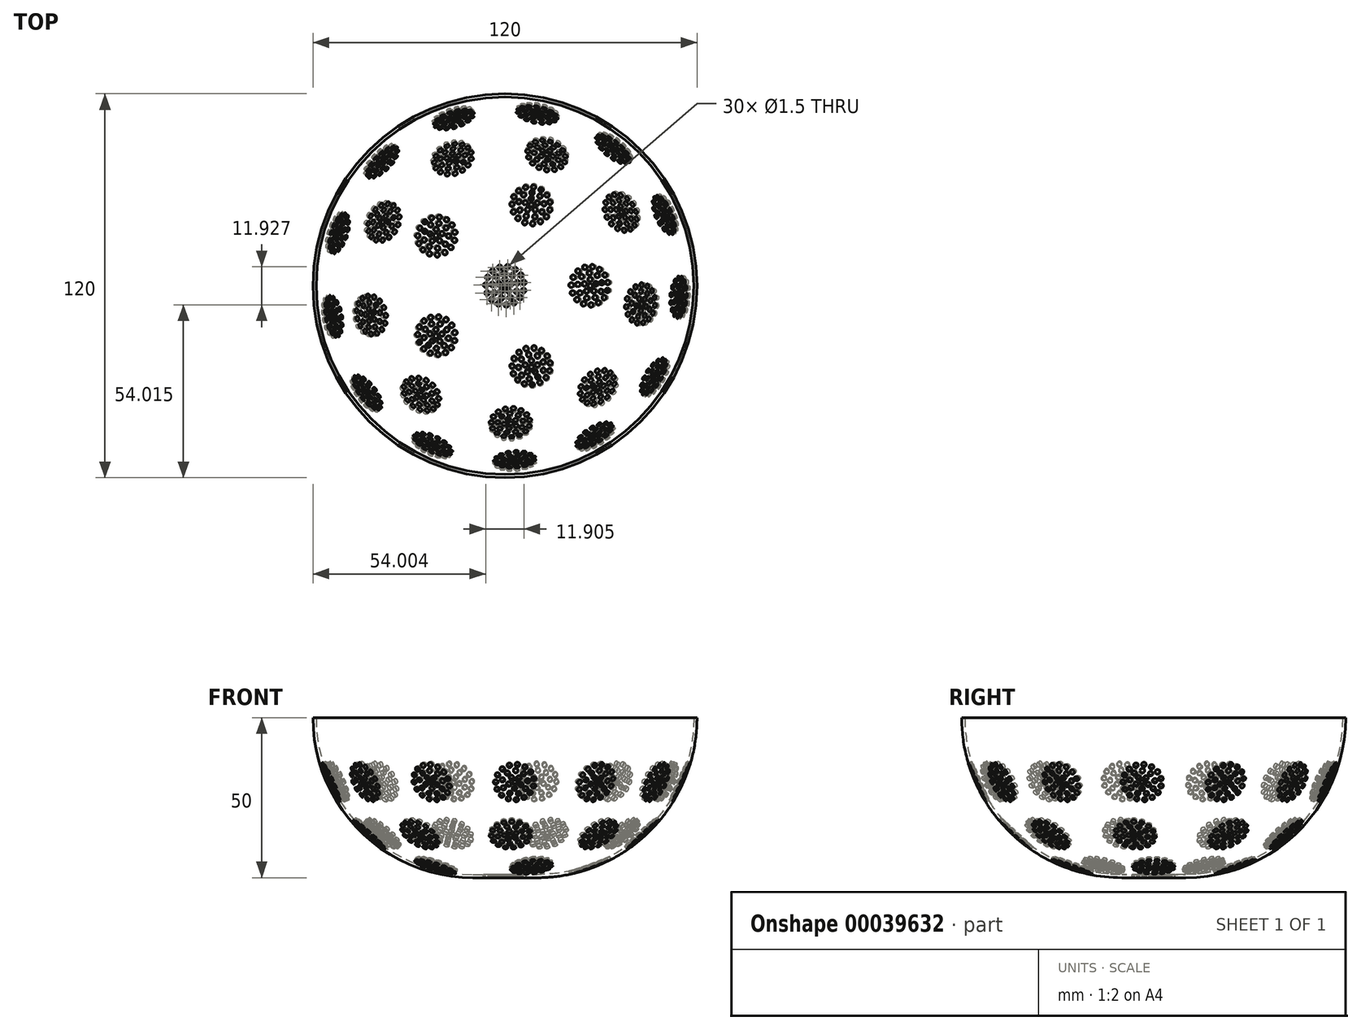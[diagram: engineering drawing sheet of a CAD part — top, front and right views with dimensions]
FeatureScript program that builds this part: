
annotation { "Feature Type Name" : "Feature", "Feature Type Description" : "" }
export const myFeature = defineFeature(function(context is Context, id is Id, definition is map)
    precondition{}
    {
        {
            var Q0;
            Q0=qCreatedBy(makeId("Front.planeOp"),FACE);
            var sketch = newSketch(context, id + "F0", { "sketchPlane" : qUnion([Q0])});
            skLineSegment(sketch, "E0", {"start": v(0, 0) * mm, "end": v(10, 0) * mm});
            skArc(sketch, "E1", {"start": v(10, 0) * mm, "mid": v(45.36, 14.64) * mm, "end": v(60, 50) * mm});
            skLineSegment(sketch, "E2", {"start": v(0, 0) * mm, "end": v(0, 50) * mm});
            skLineSegment(sketch, "E3", {"start": v(0, 50) * mm, "end": v(60, 50) * mm});
            skArc(sketch, "E4.0", {"start": v(10, 1) * mm, "mid": v(44.65, 15.35) * mm, "end": v(59, 50) * mm});
            skLineSegment(sketch, "E4.1", {"start": v(0, 1) * mm, "end": v(10, 1) * mm});
            skSolve(sketch);
        }
        {
            var Q0;
            {var subQ2=sQuery(id+"F0.wireOp",EDGE,"E0");Q0=makeQuery(id+"F0.imprint","IMPRINT",FACE,{"disambiguationData":[TD([[makeQuery(id+"F0.imprint","IMPRINT",EDGE,{"derivedFrom":subQ2}),1.0]])]});}
            var Q1;
            Q1=sQuery(id+"F0.wireOp",EDGE,"E2");
            revolve(context, id + "F1", {"entities" : qUnion([Q0]), "axis" : qUnion([Q1]), "revolveType" : RevolveType.FULL});
        }
        {
            var Q0;
            Q0=makeQuery(id+"F1.opRevolve","SWEPT_FACE",FACE,{"disambiguationData":[OSD([sQuery(id+"F0.wireOp",EDGE,"E4.1")])]});
            var sketch = newSketch(context, id + "F2", { "sketchPlane" : qUnion([Q0])});
            skCircle(sketch, "E5", {"center": v(0, 0) * mm, "radius": 0.75 * mm});
            skCircle(sketch, "E6", {"center": v(0, 2) * mm, "radius": 0.75 * mm});
            skCircle(sketch, "E7.1.0", {"center": v(-1.9, 0.62) * mm, "radius": 0.75 * mm});
            skCircle(sketch, "E7.2.0", {"center": v(-1.18, -1.62) * mm, "radius": 0.75 * mm});
            skCircle(sketch, "E7.3.0", {"center": v(1.18, -1.62) * mm, "radius": 0.75 * mm});
            skCircle(sketch, "E7.4.0", {"center": v(1.9, 0.62) * mm, "radius": 0.75 * mm});
            skLineSegment(sketch, "E8", {"start": v(0, 2) * mm, "end": v(1.9, 0.62) * mm, "construction": true});
            skLineSegment(sketch, "E9", {"start": v(0, 0) * mm, "end": v(0.95, 1.3) * mm, "construction": true});
            skLineSegment(sketch, "E10", {"start": v(0.95, 1.3) * mm, "end": v(2.35, 3.24) * mm, "construction": true});
            skCircle(sketch, "E11", {"center": v(2.35, 3.24) * mm, "radius": 0.75 * mm});
            skCircle(sketch, "E12.1.0", {"center": v(-0.28, 4) * mm, "radius": 0.75 * mm});
            skCircle(sketch, "E12.2.0", {"center": v(-2.78, 2.88) * mm, "radius": 0.75 * mm});
            skCircle(sketch, "E12.3.0", {"center": v(-3.98, 0.42) * mm, "radius": 0.75 * mm});
            skCircle(sketch, "E12.4.0", {"center": v(-3.32, -2.24) * mm, "radius": 0.75 * mm});
            skCircle(sketch, "E12.5.0", {"center": v(-1.1, -3.85) * mm, "radius": 0.75 * mm});
            skCircle(sketch, "E12.6.0", {"center": v(1.63, -3.65) * mm, "radius": 0.75 * mm});
            skCircle(sketch, "E13.1.7.0", {"center": v(3.6, -1.75) * mm, "radius": 0.75 * mm});
            skCircle(sketch, "E13.1.8.0", {"center": v(3.88, 0.97) * mm, "radius": 0.75 * mm});
            skLineSegment(sketch, "E14", {"start": v(3.88, 0.97) * mm, "end": v(2.35, 3.24) * mm, "construction": true});
            skLineSegment(sketch, "E15", {"start": v(0, 0) * mm, "end": v(3.12, 2.1) * mm, "construction": true});
            skLineSegment(sketch, "E16", {"start": v(3.12, 2.1) * mm, "end": v(4.97, 3.36) * mm, "construction": true});
            skCircle(sketch, "E17", {"center": v(4.97, 3.36) * mm, "radius": 0.75 * mm});
            skCircle(sketch, "E18.1.0", {"center": v(3.18, 5.09) * mm, "radius": 0.75 * mm});
            skCircle(sketch, "E18.2.0", {"center": v(0.84, 5.94) * mm, "radius": 0.75 * mm});
            skCircle(sketch, "E18.3.0", {"center": v(-1.65, 5.77) * mm, "radius": 0.75 * mm});
            skCircle(sketch, "E18.4.0", {"center": v(-3.86, 4.6) * mm, "radius": 0.75 * mm});
            skCircle(sketch, "E18.5.0", {"center": v(-5.4, 2.63) * mm, "radius": 0.75 * mm});
            skCircle(sketch, "E18.6.0", {"center": v(-6, 0.2) * mm, "radius": 0.75 * mm});
            skCircle(sketch, "E18.7.0", {"center": v(-5.56, -2.25) * mm, "radius": 0.75 * mm});
            skCircle(sketch, "E18.8.0", {"center": v(-4.17, -4.32) * mm, "radius": 0.75 * mm});
            skCircle(sketch, "E18.9.0", {"center": v(-2.05, -5.64) * mm, "radius": 0.75 * mm});
            skCircle(sketch, "E18.10.0", {"center": v(0.42, -5.99) * mm, "radius": 0.75 * mm});
            skCircle(sketch, "E18.11.0", {"center": v(2.82, -5.3) * mm, "radius": 0.75 * mm});
            skCircle(sketch, "E18.12.0", {"center": v(4.73, -3.7) * mm, "radius": 0.75 * mm});
            skCircle(sketch, "E18.13.0", {"center": v(5.82, -1.45) * mm, "radius": 0.75 * mm});
            skCircle(sketch, "E18.14.0", {"center": v(5.9, 1.04) * mm, "radius": 0.75 * mm});
            skSolve(sketch);
        }
        {
            var Q0;
            Q0 = qSketchRegion(id + "F2", true);
            extrude(context, id + "F3", {"entities" : qUnion([Q0]), "operationType" : NewBodyOperationType.REMOVE, "oppositeDirection" : true, "depth" : 25 * mm});
        }
        {
            var Q0;
            Q0=makeQuery(id+"F1.opRevolve","SWEPT_FACE",FACE,{"disambiguationData":[OSD([sQuery(id+"F0.wireOp",EDGE,"E3")])]});
            var sketch = newSketch(context, id + "F4", { "sketchPlane" : qUnion([Q0])});
            skLineSegment(sketch, "E19", {"start": v(0, 59) * mm, "end": v(0, -59) * mm});
            skLineSegment(sketch, "E20", {"start": v(0, 0) * mm, "end": v(-31.56, 49.85) * mm});
            skLineSegment(sketch, "E21", {"start": v(0, 0) * mm, "end": v(-46.28, 36.6) * mm});
            skSolve(sketch);
        }
        {
            var Q0;
            Q0=makeQuery(id+"F3.boolean.opBoolean","COPY",FACE,{"derivedFrom":makeQuery(id+"F3.opExtrude","SWEPT_FACE",FACE,{"disambiguationData":[OSD([sQuery(id+"F2.wireOp",EDGE,"E18.7.0")])]})});
            var Q1;
            Q1=makeQuery(id+"F3.boolean.opBoolean","COPY",FACE,{"derivedFrom":makeQuery(id+"F3.opExtrude","SWEPT_FACE",FACE,{"disambiguationData":[OSD([sQuery(id+"F2.wireOp",EDGE,"E18.6.0")])]})});
            var Q2;
            Q2=makeQuery(id+"F3.boolean.opBoolean","COPY",FACE,{"derivedFrom":makeQuery(id+"F3.opExtrude","SWEPT_FACE",FACE,{"disambiguationData":[OSD([sQuery(id+"F2.wireOp",EDGE,"E18.5.0")])]})});
            var Q3;
            Q3=makeQuery(id+"F3.boolean.opBoolean","COPY",FACE,{"derivedFrom":makeQuery(id+"F3.opExtrude","SWEPT_FACE",FACE,{"disambiguationData":[OSD([sQuery(id+"F2.wireOp",EDGE,"E18.4.0")])]})});
            var Q4;
            Q4=makeQuery(id+"F3.boolean.opBoolean","COPY",FACE,{"derivedFrom":makeQuery(id+"F3.opExtrude","SWEPT_FACE",FACE,{"disambiguationData":[OSD([sQuery(id+"F2.wireOp",EDGE,"E18.3.0")])]})});
            var Q5;
            Q5=makeQuery(id+"F3.boolean.opBoolean","COPY",FACE,{"derivedFrom":makeQuery(id+"F3.opExtrude","SWEPT_FACE",FACE,{"disambiguationData":[OSD([sQuery(id+"F2.wireOp",EDGE,"E18.2.0")])]})});
            var Q6;
            Q6=makeQuery(id+"F3.boolean.opBoolean","COPY",FACE,{"derivedFrom":makeQuery(id+"F3.opExtrude","SWEPT_FACE",FACE,{"disambiguationData":[OSD([sQuery(id+"F2.wireOp",EDGE,"E18.1.0")])]})});
            var Q7;
            Q7=makeQuery(id+"F3.boolean.opBoolean","COPY",FACE,{"derivedFrom":makeQuery(id+"F3.opExtrude","SWEPT_FACE",FACE,{"disambiguationData":[OSD([sQuery(id+"F2.wireOp",EDGE,"E17")])]})});
            var Q8;
            Q8=makeQuery(id+"F3.boolean.opBoolean","COPY",FACE,{"derivedFrom":makeQuery(id+"F3.opExtrude","SWEPT_FACE",FACE,{"disambiguationData":[OSD([sQuery(id+"F2.wireOp",EDGE,"E18.14.0")])]})});
            var Q9;
            Q9=makeQuery(id+"F3.boolean.opBoolean","COPY",FACE,{"derivedFrom":makeQuery(id+"F3.opExtrude","SWEPT_FACE",FACE,{"disambiguationData":[OSD([sQuery(id+"F2.wireOp",EDGE,"E18.13.0")])]})});
            var Q10;
            Q10=makeQuery(id+"F3.boolean.opBoolean","COPY",FACE,{"derivedFrom":makeQuery(id+"F3.opExtrude","SWEPT_FACE",FACE,{"disambiguationData":[OSD([sQuery(id+"F2.wireOp",EDGE,"E18.12.0")])]})});
            var Q11;
            Q11=makeQuery(id+"F3.boolean.opBoolean","COPY",FACE,{"derivedFrom":makeQuery(id+"F3.opExtrude","SWEPT_FACE",FACE,{"disambiguationData":[OSD([sQuery(id+"F2.wireOp",EDGE,"E18.11.0")])]})});
            var Q12;
            Q12=makeQuery(id+"F3.boolean.opBoolean","COPY",FACE,{"derivedFrom":makeQuery(id+"F3.opExtrude","SWEPT_FACE",FACE,{"disambiguationData":[OSD([sQuery(id+"F2.wireOp",EDGE,"E18.10.0")])]})});
            var Q13;
            Q13=makeQuery(id+"F3.boolean.opBoolean","COPY",FACE,{"derivedFrom":makeQuery(id+"F3.opExtrude","SWEPT_FACE",FACE,{"disambiguationData":[OSD([sQuery(id+"F2.wireOp",EDGE,"E18.9.0")])]})});
            var Q14;
            Q14=makeQuery(id+"F3.boolean.opBoolean","COPY",FACE,{"derivedFrom":makeQuery(id+"F3.opExtrude","SWEPT_FACE",FACE,{"disambiguationData":[OSD([sQuery(id+"F2.wireOp",EDGE,"E18.8.0")])]})});
            var Q15;
            Q15=makeQuery(id+"F3.boolean.opBoolean","COPY",FACE,{"derivedFrom":makeQuery(id+"F3.opExtrude","SWEPT_FACE",FACE,{"disambiguationData":[OSD([sQuery(id+"F2.wireOp",EDGE,"E12.4.0")])]})});
            var Q16;
            Q16=makeQuery(id+"F3.boolean.opBoolean","COPY",FACE,{"derivedFrom":makeQuery(id+"F3.opExtrude","SWEPT_FACE",FACE,{"disambiguationData":[OSD([sQuery(id+"F2.wireOp",EDGE,"E12.3.0")])]})});
            var Q17;
            Q17=makeQuery(id+"F3.boolean.opBoolean","COPY",FACE,{"derivedFrom":makeQuery(id+"F3.opExtrude","SWEPT_FACE",FACE,{"disambiguationData":[OSD([sQuery(id+"F2.wireOp",EDGE,"E12.2.0")])]})});
            var Q18;
            Q18=makeQuery(id+"F3.boolean.opBoolean","COPY",FACE,{"derivedFrom":makeQuery(id+"F3.opExtrude","SWEPT_FACE",FACE,{"disambiguationData":[OSD([sQuery(id+"F2.wireOp",EDGE,"E12.1.0")])]})});
            var Q19;
            Q19=makeQuery(id+"F3.boolean.opBoolean","COPY",FACE,{"derivedFrom":makeQuery(id+"F3.opExtrude","SWEPT_FACE",FACE,{"disambiguationData":[OSD([sQuery(id+"F2.wireOp",EDGE,"E11")])]})});
            var Q20;
            Q20=makeQuery(id+"F3.boolean.opBoolean","COPY",FACE,{"derivedFrom":makeQuery(id+"F3.opExtrude","SWEPT_FACE",FACE,{"disambiguationData":[OSD([sQuery(id+"F2.wireOp",EDGE,"E13.1.8.0")])]})});
            var Q21;
            Q21=makeQuery(id+"F3.boolean.opBoolean","COPY",FACE,{"derivedFrom":makeQuery(id+"F3.opExtrude","SWEPT_FACE",FACE,{"disambiguationData":[OSD([sQuery(id+"F2.wireOp",EDGE,"E13.1.7.0")])]})});
            var Q22;
            Q22=makeQuery(id+"F3.boolean.opBoolean","COPY",FACE,{"derivedFrom":makeQuery(id+"F3.opExtrude","SWEPT_FACE",FACE,{"disambiguationData":[OSD([sQuery(id+"F2.wireOp",EDGE,"E12.6.0")])]})});
            var Q23;
            Q23=makeQuery(id+"F3.boolean.opBoolean","COPY",FACE,{"derivedFrom":makeQuery(id+"F3.opExtrude","SWEPT_FACE",FACE,{"disambiguationData":[OSD([sQuery(id+"F2.wireOp",EDGE,"E12.5.0")])]})});
            var Q24;
            Q24=makeQuery(id+"F3.boolean.opBoolean","COPY",FACE,{"derivedFrom":makeQuery(id+"F3.opExtrude","SWEPT_FACE",FACE,{"disambiguationData":[OSD([sQuery(id+"F2.wireOp",EDGE,"E7.2.0")])]})});
            var Q25;
            Q25=makeQuery(id+"F3.boolean.opBoolean","COPY",FACE,{"derivedFrom":makeQuery(id+"F3.opExtrude","SWEPT_FACE",FACE,{"disambiguationData":[OSD([sQuery(id+"F2.wireOp",EDGE,"E7.1.0")])]})});
            var Q26;
            Q26=makeQuery(id+"F3.boolean.opBoolean","COPY",FACE,{"derivedFrom":makeQuery(id+"F3.opExtrude","SWEPT_FACE",FACE,{"disambiguationData":[OSD([sQuery(id+"F2.wireOp",EDGE,"E6")])]})});
            var Q27;
            Q27=makeQuery(id+"F3.boolean.opBoolean","COPY",FACE,{"derivedFrom":makeQuery(id+"F3.opExtrude","SWEPT_FACE",FACE,{"disambiguationData":[OSD([sQuery(id+"F2.wireOp",EDGE,"E7.4.0")])]})});
            var Q28;
            Q28=makeQuery(id+"F3.boolean.opBoolean","COPY",FACE,{"derivedFrom":makeQuery(id+"F3.opExtrude","SWEPT_FACE",FACE,{"disambiguationData":[OSD([sQuery(id+"F2.wireOp",EDGE,"E7.3.0")])]})});
            var Q29;
            Q29=makeQuery(id+"F3.boolean.opBoolean","COPY",FACE,{"derivedFrom":makeQuery(id+"F3.opExtrude","SWEPT_FACE",FACE,{"disambiguationData":[OSD([sQuery(id+"F2.wireOp",EDGE,"E5")])]})});
            var Q30;
            Q30=sQuery(id+"F4.wireOp",EDGE,"E19");
            circularPattern(context, id + "F5", {"faces" : qUnion([Q0, Q1, Q2, Q3, Q4, Q5, Q6, Q7, Q8, Q9, Q10, Q11, Q12, Q13, Q14, Q15, Q16, Q17, Q18, Q19, Q20, Q21, Q22, Q23, Q24, Q25, Q26, Q27, Q28, Q29]), "axis" : qUnion([Q30]), "angle" : 30 * degree, "instanceCount" : 2, "patternType" : PatternType.FACE});
        }
        {
            var Q0;
            Q0=makeQuery(id+"F5.opPattern","COPY",FACE,{"derivedFrom":makeQuery(id+"F3.boolean.opBoolean","COPY",FACE,{"derivedFrom":makeQuery(id+"F3.opExtrude","SWEPT_FACE",FACE,{"disambiguationData":[OSD([sQuery(id+"F2.wireOp",EDGE,"E18.5.0")])]})}),"instanceName":"1"});
            var Q1;
            Q1=makeQuery(id+"F5.opPattern","COPY",FACE,{"derivedFrom":makeQuery(id+"F3.boolean.opBoolean","COPY",FACE,{"derivedFrom":makeQuery(id+"F3.opExtrude","SWEPT_FACE",FACE,{"disambiguationData":[OSD([sQuery(id+"F2.wireOp",EDGE,"E18.6.0")])]})}),"instanceName":"1"});
            var Q2;
            Q2=makeQuery(id+"F5.opPattern","COPY",FACE,{"derivedFrom":makeQuery(id+"F3.boolean.opBoolean","COPY",FACE,{"derivedFrom":makeQuery(id+"F3.opExtrude","SWEPT_FACE",FACE,{"disambiguationData":[OSD([sQuery(id+"F2.wireOp",EDGE,"E18.7.0")])]})}),"instanceName":"1"});
            var Q3;
            Q3=makeQuery(id+"F5.opPattern","COPY",FACE,{"derivedFrom":makeQuery(id+"F3.boolean.opBoolean","COPY",FACE,{"derivedFrom":makeQuery(id+"F3.opExtrude","SWEPT_FACE",FACE,{"disambiguationData":[OSD([sQuery(id+"F2.wireOp",EDGE,"E18.8.0")])]})}),"instanceName":"1"});
            var Q4;
            Q4=makeQuery(id+"F5.opPattern","COPY",FACE,{"derivedFrom":makeQuery(id+"F3.boolean.opBoolean","COPY",FACE,{"derivedFrom":makeQuery(id+"F3.opExtrude","SWEPT_FACE",FACE,{"disambiguationData":[OSD([sQuery(id+"F2.wireOp",EDGE,"E18.9.0")])]})}),"instanceName":"1"});
            var Q5;
            Q5=makeQuery(id+"F5.opPattern","COPY",FACE,{"derivedFrom":makeQuery(id+"F3.boolean.opBoolean","COPY",FACE,{"derivedFrom":makeQuery(id+"F3.opExtrude","SWEPT_FACE",FACE,{"disambiguationData":[OSD([sQuery(id+"F2.wireOp",EDGE,"E18.11.0")])]})}),"instanceName":"1"});
            var Q6;
            Q6=makeQuery(id+"F5.opPattern","COPY",FACE,{"derivedFrom":makeQuery(id+"F3.boolean.opBoolean","COPY",FACE,{"derivedFrom":makeQuery(id+"F3.opExtrude","SWEPT_FACE",FACE,{"disambiguationData":[OSD([sQuery(id+"F2.wireOp",EDGE,"E18.12.0")])]})}),"instanceName":"1"});
            var Q7;
            Q7=makeQuery(id+"F5.opPattern","COPY",FACE,{"derivedFrom":makeQuery(id+"F3.boolean.opBoolean","COPY",FACE,{"derivedFrom":makeQuery(id+"F3.opExtrude","SWEPT_FACE",FACE,{"disambiguationData":[OSD([sQuery(id+"F2.wireOp",EDGE,"E18.13.0")])]})}),"instanceName":"1"});
            var Q8;
            Q8=makeQuery(id+"F5.opPattern","COPY",FACE,{"derivedFrom":makeQuery(id+"F3.boolean.opBoolean","COPY",FACE,{"derivedFrom":makeQuery(id+"F3.opExtrude","SWEPT_FACE",FACE,{"disambiguationData":[OSD([sQuery(id+"F2.wireOp",EDGE,"E18.14.0")])]})}),"instanceName":"1"});
            var Q9;
            Q9=makeQuery(id+"F5.opPattern","COPY",FACE,{"derivedFrom":makeQuery(id+"F3.boolean.opBoolean","COPY",FACE,{"derivedFrom":makeQuery(id+"F3.opExtrude","SWEPT_FACE",FACE,{"disambiguationData":[OSD([sQuery(id+"F2.wireOp",EDGE,"E17")])]})}),"instanceName":"1"});
            var Q10;
            Q10=makeQuery(id+"F5.opPattern","COPY",FACE,{"derivedFrom":makeQuery(id+"F3.boolean.opBoolean","COPY",FACE,{"derivedFrom":makeQuery(id+"F3.opExtrude","SWEPT_FACE",FACE,{"disambiguationData":[OSD([sQuery(id+"F2.wireOp",EDGE,"E18.1.0")])]})}),"instanceName":"1"});
            var Q11;
            Q11=makeQuery(id+"F5.opPattern","COPY",FACE,{"derivedFrom":makeQuery(id+"F3.boolean.opBoolean","COPY",FACE,{"derivedFrom":makeQuery(id+"F3.opExtrude","SWEPT_FACE",FACE,{"disambiguationData":[OSD([sQuery(id+"F2.wireOp",EDGE,"E18.2.0")])]})}),"instanceName":"1"});
            var Q12;
            Q12=makeQuery(id+"F5.opPattern","COPY",FACE,{"derivedFrom":makeQuery(id+"F3.boolean.opBoolean","COPY",FACE,{"derivedFrom":makeQuery(id+"F3.opExtrude","SWEPT_FACE",FACE,{"disambiguationData":[OSD([sQuery(id+"F2.wireOp",EDGE,"E18.3.0")])]})}),"instanceName":"1"});
            var Q13;
            Q13=makeQuery(id+"F5.opPattern","COPY",FACE,{"derivedFrom":makeQuery(id+"F3.boolean.opBoolean","COPY",FACE,{"derivedFrom":makeQuery(id+"F3.opExtrude","SWEPT_FACE",FACE,{"disambiguationData":[OSD([sQuery(id+"F2.wireOp",EDGE,"E18.4.0")])]})}),"instanceName":"1"});
            var Q14;
            Q14=makeQuery(id+"F5.opPattern","COPY",FACE,{"derivedFrom":makeQuery(id+"F3.boolean.opBoolean","COPY",FACE,{"derivedFrom":makeQuery(id+"F3.opExtrude","SWEPT_FACE",FACE,{"disambiguationData":[OSD([sQuery(id+"F2.wireOp",EDGE,"E12.2.0")])]})}),"instanceName":"1"});
            var Q15;
            Q15=makeQuery(id+"F5.opPattern","COPY",FACE,{"derivedFrom":makeQuery(id+"F3.boolean.opBoolean","COPY",FACE,{"derivedFrom":makeQuery(id+"F3.opExtrude","SWEPT_FACE",FACE,{"disambiguationData":[OSD([sQuery(id+"F2.wireOp",EDGE,"E12.3.0")])]})}),"instanceName":"1"});
            var Q16;
            Q16=makeQuery(id+"F5.opPattern","COPY",FACE,{"derivedFrom":makeQuery(id+"F3.boolean.opBoolean","COPY",FACE,{"derivedFrom":makeQuery(id+"F3.opExtrude","SWEPT_FACE",FACE,{"disambiguationData":[OSD([sQuery(id+"F2.wireOp",EDGE,"E12.4.0")])]})}),"instanceName":"1"});
            var Q17;
            Q17=makeQuery(id+"F5.opPattern","COPY",FACE,{"derivedFrom":makeQuery(id+"F3.boolean.opBoolean","COPY",FACE,{"derivedFrom":makeQuery(id+"F3.opExtrude","SWEPT_FACE",FACE,{"disambiguationData":[OSD([sQuery(id+"F2.wireOp",EDGE,"E12.6.0")])]})}),"instanceName":"1"});
            var Q18;
            Q18=makeQuery(id+"F5.opPattern","COPY",FACE,{"derivedFrom":makeQuery(id+"F3.boolean.opBoolean","COPY",FACE,{"derivedFrom":makeQuery(id+"F3.opExtrude","SWEPT_FACE",FACE,{"disambiguationData":[OSD([sQuery(id+"F2.wireOp",EDGE,"E13.1.7.0")])]})}),"instanceName":"1"});
            var Q19;
            Q19=makeQuery(id+"F5.opPattern","COPY",FACE,{"derivedFrom":makeQuery(id+"F3.boolean.opBoolean","COPY",FACE,{"derivedFrom":makeQuery(id+"F3.opExtrude","SWEPT_FACE",FACE,{"disambiguationData":[OSD([sQuery(id+"F2.wireOp",EDGE,"E18.10.0")])]})}),"instanceName":"1"});
            var Q20;
            Q20=makeQuery(id+"F5.opPattern","COPY",FACE,{"derivedFrom":makeQuery(id+"F3.boolean.opBoolean","COPY",FACE,{"derivedFrom":makeQuery(id+"F3.opExtrude","SWEPT_FACE",FACE,{"disambiguationData":[OSD([sQuery(id+"F2.wireOp",EDGE,"E12.5.0")])]})}),"instanceName":"1"});
            var Q21;
            Q21=makeQuery(id+"F5.opPattern","COPY",FACE,{"derivedFrom":makeQuery(id+"F3.boolean.opBoolean","COPY",FACE,{"derivedFrom":makeQuery(id+"F3.opExtrude","SWEPT_FACE",FACE,{"disambiguationData":[OSD([sQuery(id+"F2.wireOp",EDGE,"E7.2.0")])]})}),"instanceName":"1"});
            var Q22;
            Q22=makeQuery(id+"F5.opPattern","COPY",FACE,{"derivedFrom":makeQuery(id+"F3.boolean.opBoolean","COPY",FACE,{"derivedFrom":makeQuery(id+"F3.opExtrude","SWEPT_FACE",FACE,{"disambiguationData":[OSD([sQuery(id+"F2.wireOp",EDGE,"E5")])]})}),"instanceName":"1"});
            var Q23;
            Q23=makeQuery(id+"F5.opPattern","COPY",FACE,{"derivedFrom":makeQuery(id+"F3.boolean.opBoolean","COPY",FACE,{"derivedFrom":makeQuery(id+"F3.opExtrude","SWEPT_FACE",FACE,{"disambiguationData":[OSD([sQuery(id+"F2.wireOp",EDGE,"E6")])]})}),"instanceName":"1"});
            var Q24;
            Q24=makeQuery(id+"F5.opPattern","COPY",FACE,{"derivedFrom":makeQuery(id+"F3.boolean.opBoolean","COPY",FACE,{"derivedFrom":makeQuery(id+"F3.opExtrude","SWEPT_FACE",FACE,{"disambiguationData":[OSD([sQuery(id+"F2.wireOp",EDGE,"E7.4.0")])]})}),"instanceName":"1"});
            var Q25;
            Q25=makeQuery(id+"F5.opPattern","COPY",FACE,{"derivedFrom":makeQuery(id+"F3.boolean.opBoolean","COPY",FACE,{"derivedFrom":makeQuery(id+"F3.opExtrude","SWEPT_FACE",FACE,{"disambiguationData":[OSD([sQuery(id+"F2.wireOp",EDGE,"E7.3.0")])]})}),"instanceName":"1"});
            var Q26;
            Q26=makeQuery(id+"F5.opPattern","COPY",FACE,{"derivedFrom":makeQuery(id+"F3.boolean.opBoolean","COPY",FACE,{"derivedFrom":makeQuery(id+"F3.opExtrude","SWEPT_FACE",FACE,{"disambiguationData":[OSD([sQuery(id+"F2.wireOp",EDGE,"E13.1.8.0")])]})}),"instanceName":"1"});
            var Q27;
            Q27=makeQuery(id+"F5.opPattern","COPY",FACE,{"derivedFrom":makeQuery(id+"F3.boolean.opBoolean","COPY",FACE,{"derivedFrom":makeQuery(id+"F3.opExtrude","SWEPT_FACE",FACE,{"disambiguationData":[OSD([sQuery(id+"F2.wireOp",EDGE,"E11")])]})}),"instanceName":"1"});
            var Q28;
            Q28=makeQuery(id+"F5.opPattern","COPY",FACE,{"derivedFrom":makeQuery(id+"F3.boolean.opBoolean","COPY",FACE,{"derivedFrom":makeQuery(id+"F3.opExtrude","SWEPT_FACE",FACE,{"disambiguationData":[OSD([sQuery(id+"F2.wireOp",EDGE,"E12.1.0")])]})}),"instanceName":"1"});
            var Q29;
            Q29=makeQuery(id+"F5.opPattern","COPY",FACE,{"derivedFrom":makeQuery(id+"F3.boolean.opBoolean","COPY",FACE,{"derivedFrom":makeQuery(id+"F3.opExtrude","SWEPT_FACE",FACE,{"disambiguationData":[OSD([sQuery(id+"F2.wireOp",EDGE,"E7.1.0")])]})}),"instanceName":"1"});
            var Q30;
            Q30=sQuery(id+"F0.wireOp",EDGE,"E2");
            circularPattern(context, id + "F6", {"faces" : qUnion([Q0, Q1, Q2, Q3, Q4, Q5, Q6, Q7, Q8, Q9, Q10, Q11, Q12, Q13, Q14, Q15, Q16, Q17, Q18, Q19, Q20, Q21, Q22, Q23, Q24, Q25, Q26, Q27, Q28, Q29]), "axis" : qUnion([Q30]), "angle" : 360 * degree, "instanceCount" : 5, "equalSpace" : true, "patternType" : PatternType.FACE});
        }
        {
            var Q0;
            Q0=makeQuery(id+"F3.boolean.opBoolean","COPY",FACE,{"derivedFrom":makeQuery(id+"F3.opExtrude","SWEPT_FACE",FACE,{"disambiguationData":[OSD([sQuery(id+"F2.wireOp",EDGE,"E18.1.0")])]})});
            var Q1;
            Q1=makeQuery(id+"F3.boolean.opBoolean","COPY",FACE,{"derivedFrom":makeQuery(id+"F3.opExtrude","SWEPT_FACE",FACE,{"disambiguationData":[OSD([sQuery(id+"F2.wireOp",EDGE,"E18.2.0")])]})});
            var Q2;
            Q2=makeQuery(id+"F3.boolean.opBoolean","COPY",FACE,{"derivedFrom":makeQuery(id+"F3.opExtrude","SWEPT_FACE",FACE,{"disambiguationData":[OSD([sQuery(id+"F2.wireOp",EDGE,"E18.3.0")])]})});
            var Q3;
            Q3=makeQuery(id+"F3.boolean.opBoolean","COPY",FACE,{"derivedFrom":makeQuery(id+"F3.opExtrude","SWEPT_FACE",FACE,{"disambiguationData":[OSD([sQuery(id+"F2.wireOp",EDGE,"E18.4.0")])]})});
            var Q4;
            Q4=makeQuery(id+"F3.boolean.opBoolean","COPY",FACE,{"derivedFrom":makeQuery(id+"F3.opExtrude","SWEPT_FACE",FACE,{"disambiguationData":[OSD([sQuery(id+"F2.wireOp",EDGE,"E18.5.0")])]})});
            var Q5;
            Q5=makeQuery(id+"F3.boolean.opBoolean","COPY",FACE,{"derivedFrom":makeQuery(id+"F3.opExtrude","SWEPT_FACE",FACE,{"disambiguationData":[OSD([sQuery(id+"F2.wireOp",EDGE,"E18.6.0")])]})});
            var Q6;
            Q6=makeQuery(id+"F3.boolean.opBoolean","COPY",FACE,{"derivedFrom":makeQuery(id+"F3.opExtrude","SWEPT_FACE",FACE,{"disambiguationData":[OSD([sQuery(id+"F2.wireOp",EDGE,"E18.7.0")])]})});
            var Q7;
            Q7=makeQuery(id+"F3.boolean.opBoolean","COPY",FACE,{"derivedFrom":makeQuery(id+"F3.opExtrude","SWEPT_FACE",FACE,{"disambiguationData":[OSD([sQuery(id+"F2.wireOp",EDGE,"E18.8.0")])]})});
            var Q8;
            Q8=makeQuery(id+"F3.boolean.opBoolean","COPY",FACE,{"derivedFrom":makeQuery(id+"F3.opExtrude","SWEPT_FACE",FACE,{"disambiguationData":[OSD([sQuery(id+"F2.wireOp",EDGE,"E18.9.0")])]})});
            var Q9;
            Q9=makeQuery(id+"F3.boolean.opBoolean","COPY",FACE,{"derivedFrom":makeQuery(id+"F3.opExtrude","SWEPT_FACE",FACE,{"disambiguationData":[OSD([sQuery(id+"F2.wireOp",EDGE,"E18.10.0")])]})});
            var Q10;
            Q10=makeQuery(id+"F3.boolean.opBoolean","COPY",FACE,{"derivedFrom":makeQuery(id+"F3.opExtrude","SWEPT_FACE",FACE,{"disambiguationData":[OSD([sQuery(id+"F2.wireOp",EDGE,"E18.11.0")])]})});
            var Q11;
            Q11=makeQuery(id+"F3.boolean.opBoolean","COPY",FACE,{"derivedFrom":makeQuery(id+"F3.opExtrude","SWEPT_FACE",FACE,{"disambiguationData":[OSD([sQuery(id+"F2.wireOp",EDGE,"E18.12.0")])]})});
            var Q12;
            Q12=makeQuery(id+"F3.boolean.opBoolean","COPY",FACE,{"derivedFrom":makeQuery(id+"F3.opExtrude","SWEPT_FACE",FACE,{"disambiguationData":[OSD([sQuery(id+"F2.wireOp",EDGE,"E18.13.0")])]})});
            var Q13;
            Q13=makeQuery(id+"F3.boolean.opBoolean","COPY",FACE,{"derivedFrom":makeQuery(id+"F3.opExtrude","SWEPT_FACE",FACE,{"disambiguationData":[OSD([sQuery(id+"F2.wireOp",EDGE,"E18.14.0")])]})});
            var Q14;
            Q14=makeQuery(id+"F3.boolean.opBoolean","COPY",FACE,{"derivedFrom":makeQuery(id+"F3.opExtrude","SWEPT_FACE",FACE,{"disambiguationData":[OSD([sQuery(id+"F2.wireOp",EDGE,"E13.1.8.0")])]})});
            var Q15;
            Q15=makeQuery(id+"F3.boolean.opBoolean","COPY",FACE,{"derivedFrom":makeQuery(id+"F3.opExtrude","SWEPT_FACE",FACE,{"disambiguationData":[OSD([sQuery(id+"F2.wireOp",EDGE,"E11")])]})});
            var Q16;
            Q16=makeQuery(id+"F3.boolean.opBoolean","COPY",FACE,{"derivedFrom":makeQuery(id+"F3.opExtrude","SWEPT_FACE",FACE,{"disambiguationData":[OSD([sQuery(id+"F2.wireOp",EDGE,"E12.1.0")])]})});
            var Q17;
            Q17=makeQuery(id+"F3.boolean.opBoolean","COPY",FACE,{"derivedFrom":makeQuery(id+"F3.opExtrude","SWEPT_FACE",FACE,{"disambiguationData":[OSD([sQuery(id+"F2.wireOp",EDGE,"E12.2.0")])]})});
            var Q18;
            Q18=makeQuery(id+"F3.boolean.opBoolean","COPY",FACE,{"derivedFrom":makeQuery(id+"F3.opExtrude","SWEPT_FACE",FACE,{"disambiguationData":[OSD([sQuery(id+"F2.wireOp",EDGE,"E12.3.0")])]})});
            var Q19;
            Q19=makeQuery(id+"F3.boolean.opBoolean","COPY",FACE,{"derivedFrom":makeQuery(id+"F3.opExtrude","SWEPT_FACE",FACE,{"disambiguationData":[OSD([sQuery(id+"F2.wireOp",EDGE,"E12.4.0")])]})});
            var Q20;
            Q20=makeQuery(id+"F3.boolean.opBoolean","COPY",FACE,{"derivedFrom":makeQuery(id+"F3.opExtrude","SWEPT_FACE",FACE,{"disambiguationData":[OSD([sQuery(id+"F2.wireOp",EDGE,"E12.5.0")])]})});
            var Q21;
            Q21=makeQuery(id+"F3.boolean.opBoolean","COPY",FACE,{"derivedFrom":makeQuery(id+"F3.opExtrude","SWEPT_FACE",FACE,{"disambiguationData":[OSD([sQuery(id+"F2.wireOp",EDGE,"E12.6.0")])]})});
            var Q22;
            Q22=makeQuery(id+"F3.boolean.opBoolean","COPY",FACE,{"derivedFrom":makeQuery(id+"F3.opExtrude","SWEPT_FACE",FACE,{"disambiguationData":[OSD([sQuery(id+"F2.wireOp",EDGE,"E13.1.7.0")])]})});
            var Q23;
            Q23=makeQuery(id+"F3.boolean.opBoolean","COPY",FACE,{"derivedFrom":makeQuery(id+"F3.opExtrude","SWEPT_FACE",FACE,{"disambiguationData":[OSD([sQuery(id+"F2.wireOp",EDGE,"E7.4.0")])]})});
            var Q24;
            Q24=makeQuery(id+"F3.boolean.opBoolean","COPY",FACE,{"derivedFrom":makeQuery(id+"F3.opExtrude","SWEPT_FACE",FACE,{"disambiguationData":[OSD([sQuery(id+"F2.wireOp",EDGE,"E6")])]})});
            var Q25;
            Q25=makeQuery(id+"F3.boolean.opBoolean","COPY",FACE,{"derivedFrom":makeQuery(id+"F3.opExtrude","SWEPT_FACE",FACE,{"disambiguationData":[OSD([sQuery(id+"F2.wireOp",EDGE,"E7.1.0")])]})});
            var Q26;
            Q26=makeQuery(id+"F3.boolean.opBoolean","COPY",FACE,{"derivedFrom":makeQuery(id+"F3.opExtrude","SWEPT_FACE",FACE,{"disambiguationData":[OSD([sQuery(id+"F2.wireOp",EDGE,"E7.2.0")])]})});
            var Q27;
            Q27=makeQuery(id+"F3.boolean.opBoolean","COPY",FACE,{"derivedFrom":makeQuery(id+"F3.opExtrude","SWEPT_FACE",FACE,{"disambiguationData":[OSD([sQuery(id+"F2.wireOp",EDGE,"E5")])]})});
            var Q28;
            Q28=makeQuery(id+"F3.boolean.opBoolean","COPY",FACE,{"derivedFrom":makeQuery(id+"F3.opExtrude","SWEPT_FACE",FACE,{"disambiguationData":[OSD([sQuery(id+"F2.wireOp",EDGE,"E7.3.0")])]})});
            var Q29;
            Q29=makeQuery(id+"F3.boolean.opBoolean","COPY",FACE,{"derivedFrom":makeQuery(id+"F3.opExtrude","SWEPT_FACE",FACE,{"disambiguationData":[OSD([sQuery(id+"F2.wireOp",EDGE,"E17")])]})});
            var Q30;
            Q30=sQuery(id+"F4.wireOp",EDGE,"E20");
            circularPattern(context, id + "F7", {"faces" : qUnion([Q0, Q1, Q2, Q3, Q4, Q5, Q6, Q7, Q8, Q9, Q10, Q11, Q12, Q13, Q14, Q15, Q16, Q17, Q18, Q19, Q20, Q21, Q22, Q23, Q24, Q25, Q26, Q27, Q28, Q29]), "axis" : qUnion([Q30]), "angle" : 50 * degree, "instanceCount" : 2, "oppositeDirection" : true, "patternType" : PatternType.FACE});
        }
        {
            var Q0;
            Q0=makeQuery(id+"F7.opPattern","COPY",FACE,{"derivedFrom":makeQuery(id+"F3.boolean.opBoolean","COPY",FACE,{"derivedFrom":makeQuery(id+"F3.opExtrude","SWEPT_FACE",FACE,{"disambiguationData":[OSD([sQuery(id+"F2.wireOp",EDGE,"E18.10.0")])]})}),"instanceName":"1"});
            var Q1;
            Q1=makeQuery(id+"F7.opPattern","COPY",FACE,{"derivedFrom":makeQuery(id+"F3.boolean.opBoolean","COPY",FACE,{"derivedFrom":makeQuery(id+"F3.opExtrude","SWEPT_FACE",FACE,{"disambiguationData":[OSD([sQuery(id+"F2.wireOp",EDGE,"E18.9.0")])]})}),"instanceName":"1"});
            var Q2;
            Q2=makeQuery(id+"F7.opPattern","COPY",FACE,{"derivedFrom":makeQuery(id+"F3.boolean.opBoolean","COPY",FACE,{"derivedFrom":makeQuery(id+"F3.opExtrude","SWEPT_FACE",FACE,{"disambiguationData":[OSD([sQuery(id+"F2.wireOp",EDGE,"E18.8.0")])]})}),"instanceName":"1"});
            var Q3;
            Q3=makeQuery(id+"F7.opPattern","COPY",FACE,{"derivedFrom":makeQuery(id+"F3.boolean.opBoolean","COPY",FACE,{"derivedFrom":makeQuery(id+"F3.opExtrude","SWEPT_FACE",FACE,{"disambiguationData":[OSD([sQuery(id+"F2.wireOp",EDGE,"E18.7.0")])]})}),"instanceName":"1"});
            var Q4;
            Q4=makeQuery(id+"F7.opPattern","COPY",FACE,{"derivedFrom":makeQuery(id+"F3.boolean.opBoolean","COPY",FACE,{"derivedFrom":makeQuery(id+"F3.opExtrude","SWEPT_FACE",FACE,{"disambiguationData":[OSD([sQuery(id+"F2.wireOp",EDGE,"E18.6.0")])]})}),"instanceName":"1"});
            var Q5;
            Q5=makeQuery(id+"F7.opPattern","COPY",FACE,{"derivedFrom":makeQuery(id+"F3.boolean.opBoolean","COPY",FACE,{"derivedFrom":makeQuery(id+"F3.opExtrude","SWEPT_FACE",FACE,{"disambiguationData":[OSD([sQuery(id+"F2.wireOp",EDGE,"E18.5.0")])]})}),"instanceName":"1"});
            var Q6;
            Q6=makeQuery(id+"F7.opPattern","COPY",FACE,{"derivedFrom":makeQuery(id+"F3.boolean.opBoolean","COPY",FACE,{"derivedFrom":makeQuery(id+"F3.opExtrude","SWEPT_FACE",FACE,{"disambiguationData":[OSD([sQuery(id+"F2.wireOp",EDGE,"E18.4.0")])]})}),"instanceName":"1"});
            var Q7;
            Q7=makeQuery(id+"F7.opPattern","COPY",FACE,{"derivedFrom":makeQuery(id+"F3.boolean.opBoolean","COPY",FACE,{"derivedFrom":makeQuery(id+"F3.opExtrude","SWEPT_FACE",FACE,{"disambiguationData":[OSD([sQuery(id+"F2.wireOp",EDGE,"E18.3.0")])]})}),"instanceName":"1"});
            var Q8;
            Q8=makeQuery(id+"F7.opPattern","COPY",FACE,{"derivedFrom":makeQuery(id+"F3.boolean.opBoolean","COPY",FACE,{"derivedFrom":makeQuery(id+"F3.opExtrude","SWEPT_FACE",FACE,{"disambiguationData":[OSD([sQuery(id+"F2.wireOp",EDGE,"E12.2.0")])]})}),"instanceName":"1"});
            var Q9;
            Q9=makeQuery(id+"F7.opPattern","COPY",FACE,{"derivedFrom":makeQuery(id+"F3.boolean.opBoolean","COPY",FACE,{"derivedFrom":makeQuery(id+"F3.opExtrude","SWEPT_FACE",FACE,{"disambiguationData":[OSD([sQuery(id+"F2.wireOp",EDGE,"E12.3.0")])]})}),"instanceName":"1"});
            var Q10;
            Q10=makeQuery(id+"F7.opPattern","COPY",FACE,{"derivedFrom":makeQuery(id+"F3.boolean.opBoolean","COPY",FACE,{"derivedFrom":makeQuery(id+"F3.opExtrude","SWEPT_FACE",FACE,{"disambiguationData":[OSD([sQuery(id+"F2.wireOp",EDGE,"E12.4.0")])]})}),"instanceName":"1"});
            var Q11;
            Q11=makeQuery(id+"F7.opPattern","COPY",FACE,{"derivedFrom":makeQuery(id+"F3.boolean.opBoolean","COPY",FACE,{"derivedFrom":makeQuery(id+"F3.opExtrude","SWEPT_FACE",FACE,{"disambiguationData":[OSD([sQuery(id+"F2.wireOp",EDGE,"E12.5.0")])]})}),"instanceName":"1"});
            var Q12;
            Q12=makeQuery(id+"F7.opPattern","COPY",FACE,{"derivedFrom":makeQuery(id+"F3.boolean.opBoolean","COPY",FACE,{"derivedFrom":makeQuery(id+"F3.opExtrude","SWEPT_FACE",FACE,{"disambiguationData":[OSD([sQuery(id+"F2.wireOp",EDGE,"E12.6.0")])]})}),"instanceName":"1"});
            var Q13;
            Q13=makeQuery(id+"F7.opPattern","COPY",FACE,{"derivedFrom":makeQuery(id+"F3.boolean.opBoolean","COPY",FACE,{"derivedFrom":makeQuery(id+"F3.opExtrude","SWEPT_FACE",FACE,{"disambiguationData":[OSD([sQuery(id+"F2.wireOp",EDGE,"E7.2.0")])]})}),"instanceName":"1"});
            var Q14;
            Q14=makeQuery(id+"F7.opPattern","COPY",FACE,{"derivedFrom":makeQuery(id+"F3.boolean.opBoolean","COPY",FACE,{"derivedFrom":makeQuery(id+"F3.opExtrude","SWEPT_FACE",FACE,{"disambiguationData":[OSD([sQuery(id+"F2.wireOp",EDGE,"E7.1.0")])]})}),"instanceName":"1"});
            var Q15;
            Q15=makeQuery(id+"F7.opPattern","COPY",FACE,{"derivedFrom":makeQuery(id+"F3.boolean.opBoolean","COPY",FACE,{"derivedFrom":makeQuery(id+"F3.opExtrude","SWEPT_FACE",FACE,{"disambiguationData":[OSD([sQuery(id+"F2.wireOp",EDGE,"E6")])]})}),"instanceName":"1"});
            var Q16;
            Q16=makeQuery(id+"F7.opPattern","COPY",FACE,{"derivedFrom":makeQuery(id+"F3.boolean.opBoolean","COPY",FACE,{"derivedFrom":makeQuery(id+"F3.opExtrude","SWEPT_FACE",FACE,{"disambiguationData":[OSD([sQuery(id+"F2.wireOp",EDGE,"E12.1.0")])]})}),"instanceName":"1"});
            var Q17;
            Q17=makeQuery(id+"F7.opPattern","COPY",FACE,{"derivedFrom":makeQuery(id+"F3.boolean.opBoolean","COPY",FACE,{"derivedFrom":makeQuery(id+"F3.opExtrude","SWEPT_FACE",FACE,{"disambiguationData":[OSD([sQuery(id+"F2.wireOp",EDGE,"E18.2.0")])]})}),"instanceName":"1"});
            var Q18;
            Q18=makeQuery(id+"F7.opPattern","COPY",FACE,{"derivedFrom":makeQuery(id+"F3.boolean.opBoolean","COPY",FACE,{"derivedFrom":makeQuery(id+"F3.opExtrude","SWEPT_FACE",FACE,{"disambiguationData":[OSD([sQuery(id+"F2.wireOp",EDGE,"E18.1.0")])]})}),"instanceName":"1"});
            var Q19;
            Q19=makeQuery(id+"F7.opPattern","COPY",FACE,{"derivedFrom":makeQuery(id+"F3.boolean.opBoolean","COPY",FACE,{"derivedFrom":makeQuery(id+"F3.opExtrude","SWEPT_FACE",FACE,{"disambiguationData":[OSD([sQuery(id+"F2.wireOp",EDGE,"E11")])]})}),"instanceName":"1"});
            var Q20;
            Q20=makeQuery(id+"F7.opPattern","COPY",FACE,{"derivedFrom":makeQuery(id+"F3.boolean.opBoolean","COPY",FACE,{"derivedFrom":makeQuery(id+"F3.opExtrude","SWEPT_FACE",FACE,{"disambiguationData":[OSD([sQuery(id+"F2.wireOp",EDGE,"E7.4.0")])]})}),"instanceName":"1"});
            var Q21;
            Q21=makeQuery(id+"F7.opPattern","COPY",FACE,{"derivedFrom":makeQuery(id+"F3.boolean.opBoolean","COPY",FACE,{"derivedFrom":makeQuery(id+"F3.opExtrude","SWEPT_FACE",FACE,{"disambiguationData":[OSD([sQuery(id+"F2.wireOp",EDGE,"E5")])]})}),"instanceName":"1"});
            var Q22;
            Q22=makeQuery(id+"F7.opPattern","COPY",FACE,{"derivedFrom":makeQuery(id+"F3.boolean.opBoolean","COPY",FACE,{"derivedFrom":makeQuery(id+"F3.opExtrude","SWEPT_FACE",FACE,{"disambiguationData":[OSD([sQuery(id+"F2.wireOp",EDGE,"E7.3.0")])]})}),"instanceName":"1"});
            var Q23;
            Q23=makeQuery(id+"F7.opPattern","COPY",FACE,{"derivedFrom":makeQuery(id+"F3.boolean.opBoolean","COPY",FACE,{"derivedFrom":makeQuery(id+"F3.opExtrude","SWEPT_FACE",FACE,{"disambiguationData":[OSD([sQuery(id+"F2.wireOp",EDGE,"E18.11.0")])]})}),"instanceName":"1"});
            var Q24;
            Q24=makeQuery(id+"F7.opPattern","COPY",FACE,{"derivedFrom":makeQuery(id+"F3.boolean.opBoolean","COPY",FACE,{"derivedFrom":makeQuery(id+"F3.opExtrude","SWEPT_FACE",FACE,{"disambiguationData":[OSD([sQuery(id+"F2.wireOp",EDGE,"E18.12.0")])]})}),"instanceName":"1"});
            var Q25;
            Q25=makeQuery(id+"F7.opPattern","COPY",FACE,{"derivedFrom":makeQuery(id+"F3.boolean.opBoolean","COPY",FACE,{"derivedFrom":makeQuery(id+"F3.opExtrude","SWEPT_FACE",FACE,{"disambiguationData":[OSD([sQuery(id+"F2.wireOp",EDGE,"E13.1.7.0")])]})}),"instanceName":"1"});
            var Q26;
            Q26=makeQuery(id+"F7.opPattern","COPY",FACE,{"derivedFrom":makeQuery(id+"F3.boolean.opBoolean","COPY",FACE,{"derivedFrom":makeQuery(id+"F3.opExtrude","SWEPT_FACE",FACE,{"disambiguationData":[OSD([sQuery(id+"F2.wireOp",EDGE,"E18.13.0")])]})}),"instanceName":"1"});
            var Q27;
            Q27=makeQuery(id+"F7.opPattern","COPY",FACE,{"derivedFrom":makeQuery(id+"F3.boolean.opBoolean","COPY",FACE,{"derivedFrom":makeQuery(id+"F3.opExtrude","SWEPT_FACE",FACE,{"disambiguationData":[OSD([sQuery(id+"F2.wireOp",EDGE,"E18.14.0")])]})}),"instanceName":"1"});
            var Q28;
            Q28=makeQuery(id+"F7.opPattern","COPY",FACE,{"derivedFrom":makeQuery(id+"F3.boolean.opBoolean","COPY",FACE,{"derivedFrom":makeQuery(id+"F3.opExtrude","SWEPT_FACE",FACE,{"disambiguationData":[OSD([sQuery(id+"F2.wireOp",EDGE,"E13.1.8.0")])]})}),"instanceName":"1"});
            var Q29;
            Q29=makeQuery(id+"F7.opPattern","COPY",FACE,{"derivedFrom":makeQuery(id+"F3.boolean.opBoolean","COPY",FACE,{"derivedFrom":makeQuery(id+"F3.opExtrude","SWEPT_FACE",FACE,{"disambiguationData":[OSD([sQuery(id+"F2.wireOp",EDGE,"E17")])]})}),"instanceName":"1"});
            var Q30;
            Q30=sQuery(id+"F0.wireOp",EDGE,"E2");
            circularPattern(context, id + "F8", {"faces" : qUnion([Q0, Q1, Q2, Q3, Q4, Q5, Q6, Q7, Q8, Q9, Q10, Q11, Q12, Q13, Q14, Q15, Q16, Q17, Q18, Q19, Q20, Q21, Q22, Q23, Q24, Q25, Q26, Q27, Q28, Q29]), "axis" : qUnion([Q30]), "angle" : 360 * degree, "instanceCount" : 9, "equalSpace" : true, "patternType" : PatternType.FACE});
        }
        {
            var Q0;
            Q0=makeQuery(id+"F3.boolean.opBoolean","COPY",FACE,{"derivedFrom":makeQuery(id+"F3.opExtrude","SWEPT_FACE",FACE,{"disambiguationData":[OSD([sQuery(id+"F2.wireOp",EDGE,"E18.14.0")])]})});
            var Q1;
            Q1=makeQuery(id+"F3.boolean.opBoolean","COPY",FACE,{"derivedFrom":makeQuery(id+"F3.opExtrude","SWEPT_FACE",FACE,{"disambiguationData":[OSD([sQuery(id+"F2.wireOp",EDGE,"E17")])]})});
            var Q2;
            Q2=makeQuery(id+"F3.boolean.opBoolean","COPY",FACE,{"derivedFrom":makeQuery(id+"F3.opExtrude","SWEPT_FACE",FACE,{"disambiguationData":[OSD([sQuery(id+"F2.wireOp",EDGE,"E18.1.0")])]})});
            var Q3;
            Q3=makeQuery(id+"F3.boolean.opBoolean","COPY",FACE,{"derivedFrom":makeQuery(id+"F3.opExtrude","SWEPT_FACE",FACE,{"disambiguationData":[OSD([sQuery(id+"F2.wireOp",EDGE,"E18.2.0")])]})});
            var Q4;
            Q4=makeQuery(id+"F3.boolean.opBoolean","COPY",FACE,{"derivedFrom":makeQuery(id+"F3.opExtrude","SWEPT_FACE",FACE,{"disambiguationData":[OSD([sQuery(id+"F2.wireOp",EDGE,"E18.3.0")])]})});
            var Q5;
            Q5=makeQuery(id+"F3.boolean.opBoolean","COPY",FACE,{"derivedFrom":makeQuery(id+"F3.opExtrude","SWEPT_FACE",FACE,{"disambiguationData":[OSD([sQuery(id+"F2.wireOp",EDGE,"E18.4.0")])]})});
            var Q6;
            Q6=makeQuery(id+"F3.boolean.opBoolean","COPY",FACE,{"derivedFrom":makeQuery(id+"F3.opExtrude","SWEPT_FACE",FACE,{"disambiguationData":[OSD([sQuery(id+"F2.wireOp",EDGE,"E18.5.0")])]})});
            var Q7;
            Q7=makeQuery(id+"F3.boolean.opBoolean","COPY",FACE,{"derivedFrom":makeQuery(id+"F3.opExtrude","SWEPT_FACE",FACE,{"disambiguationData":[OSD([sQuery(id+"F2.wireOp",EDGE,"E18.6.0")])]})});
            var Q8;
            Q8=makeQuery(id+"F3.boolean.opBoolean","COPY",FACE,{"derivedFrom":makeQuery(id+"F3.opExtrude","SWEPT_FACE",FACE,{"disambiguationData":[OSD([sQuery(id+"F2.wireOp",EDGE,"E18.7.0")])]})});
            var Q9;
            Q9=makeQuery(id+"F3.boolean.opBoolean","COPY",FACE,{"derivedFrom":makeQuery(id+"F3.opExtrude","SWEPT_FACE",FACE,{"disambiguationData":[OSD([sQuery(id+"F2.wireOp",EDGE,"E18.8.0")])]})});
            var Q10;
            Q10=makeQuery(id+"F3.boolean.opBoolean","COPY",FACE,{"derivedFrom":makeQuery(id+"F3.opExtrude","SWEPT_FACE",FACE,{"disambiguationData":[OSD([sQuery(id+"F2.wireOp",EDGE,"E18.9.0")])]})});
            var Q11;
            Q11=makeQuery(id+"F3.boolean.opBoolean","COPY",FACE,{"derivedFrom":makeQuery(id+"F3.opExtrude","SWEPT_FACE",FACE,{"disambiguationData":[OSD([sQuery(id+"F2.wireOp",EDGE,"E18.10.0")])]})});
            var Q12;
            Q12=makeQuery(id+"F3.boolean.opBoolean","COPY",FACE,{"derivedFrom":makeQuery(id+"F3.opExtrude","SWEPT_FACE",FACE,{"disambiguationData":[OSD([sQuery(id+"F2.wireOp",EDGE,"E18.11.0")])]})});
            var Q13;
            Q13=makeQuery(id+"F3.boolean.opBoolean","COPY",FACE,{"derivedFrom":makeQuery(id+"F3.opExtrude","SWEPT_FACE",FACE,{"disambiguationData":[OSD([sQuery(id+"F2.wireOp",EDGE,"E18.12.0")])]})});
            var Q14;
            Q14=makeQuery(id+"F3.boolean.opBoolean","COPY",FACE,{"derivedFrom":makeQuery(id+"F3.opExtrude","SWEPT_FACE",FACE,{"disambiguationData":[OSD([sQuery(id+"F2.wireOp",EDGE,"E18.13.0")])]})});
            var Q15;
            Q15=makeQuery(id+"F3.boolean.opBoolean","COPY",FACE,{"derivedFrom":makeQuery(id+"F3.opExtrude","SWEPT_FACE",FACE,{"disambiguationData":[OSD([sQuery(id+"F2.wireOp",EDGE,"E13.1.8.0")])]})});
            var Q16;
            Q16=makeQuery(id+"F3.boolean.opBoolean","COPY",FACE,{"derivedFrom":makeQuery(id+"F3.opExtrude","SWEPT_FACE",FACE,{"disambiguationData":[OSD([sQuery(id+"F2.wireOp",EDGE,"E11")])]})});
            var Q17;
            Q17=makeQuery(id+"F3.boolean.opBoolean","COPY",FACE,{"derivedFrom":makeQuery(id+"F3.opExtrude","SWEPT_FACE",FACE,{"disambiguationData":[OSD([sQuery(id+"F2.wireOp",EDGE,"E12.1.0")])]})});
            var Q18;
            Q18=makeQuery(id+"F3.boolean.opBoolean","COPY",FACE,{"derivedFrom":makeQuery(id+"F3.opExtrude","SWEPT_FACE",FACE,{"disambiguationData":[OSD([sQuery(id+"F2.wireOp",EDGE,"E6")])]})});
            var Q19;
            Q19=makeQuery(id+"F3.boolean.opBoolean","COPY",FACE,{"derivedFrom":makeQuery(id+"F3.opExtrude","SWEPT_FACE",FACE,{"disambiguationData":[OSD([sQuery(id+"F2.wireOp",EDGE,"E7.4.0")])]})});
            var Q20;
            Q20=makeQuery(id+"F3.boolean.opBoolean","COPY",FACE,{"derivedFrom":makeQuery(id+"F3.opExtrude","SWEPT_FACE",FACE,{"disambiguationData":[OSD([sQuery(id+"F2.wireOp",EDGE,"E13.1.7.0")])]})});
            var Q21;
            Q21=makeQuery(id+"F3.boolean.opBoolean","COPY",FACE,{"derivedFrom":makeQuery(id+"F3.opExtrude","SWEPT_FACE",FACE,{"disambiguationData":[OSD([sQuery(id+"F2.wireOp",EDGE,"E7.3.0")])]})});
            var Q22;
            Q22=makeQuery(id+"F3.boolean.opBoolean","COPY",FACE,{"derivedFrom":makeQuery(id+"F3.opExtrude","SWEPT_FACE",FACE,{"disambiguationData":[OSD([sQuery(id+"F2.wireOp",EDGE,"E5")])]})});
            var Q23;
            Q23=makeQuery(id+"F3.boolean.opBoolean","COPY",FACE,{"derivedFrom":makeQuery(id+"F3.opExtrude","SWEPT_FACE",FACE,{"disambiguationData":[OSD([sQuery(id+"F2.wireOp",EDGE,"E12.2.0")])]})});
            var Q24;
            Q24=makeQuery(id+"F3.boolean.opBoolean","COPY",FACE,{"derivedFrom":makeQuery(id+"F3.opExtrude","SWEPT_FACE",FACE,{"disambiguationData":[OSD([sQuery(id+"F2.wireOp",EDGE,"E7.1.0")])]})});
            var Q25;
            Q25=makeQuery(id+"F3.boolean.opBoolean","COPY",FACE,{"derivedFrom":makeQuery(id+"F3.opExtrude","SWEPT_FACE",FACE,{"disambiguationData":[OSD([sQuery(id+"F2.wireOp",EDGE,"E7.2.0")])]})});
            var Q26;
            Q26=makeQuery(id+"F3.boolean.opBoolean","COPY",FACE,{"derivedFrom":makeQuery(id+"F3.opExtrude","SWEPT_FACE",FACE,{"disambiguationData":[OSD([sQuery(id+"F2.wireOp",EDGE,"E12.5.0")])]})});
            var Q27;
            Q27=makeQuery(id+"F3.boolean.opBoolean","COPY",FACE,{"derivedFrom":makeQuery(id+"F3.opExtrude","SWEPT_FACE",FACE,{"disambiguationData":[OSD([sQuery(id+"F2.wireOp",EDGE,"E12.4.0")])]})});
            var Q28;
            Q28=makeQuery(id+"F3.boolean.opBoolean","COPY",FACE,{"derivedFrom":makeQuery(id+"F3.opExtrude","SWEPT_FACE",FACE,{"disambiguationData":[OSD([sQuery(id+"F2.wireOp",EDGE,"E12.3.0")])]})});
            var Q29;
            Q29=makeQuery(id+"F3.boolean.opBoolean","COPY",FACE,{"derivedFrom":makeQuery(id+"F3.opExtrude","SWEPT_FACE",FACE,{"disambiguationData":[OSD([sQuery(id+"F2.wireOp",EDGE,"E12.6.0")])]})});
            var Q30;
            Q30=sQuery(id+"F4.wireOp",EDGE,"E21");
            circularPattern(context, id + "F9", {"faces" : qUnion([Q0, Q1, Q2, Q3, Q4, Q5, Q6, Q7, Q8, Q9, Q10, Q11, Q12, Q13, Q14, Q15, Q16, Q17, Q18, Q19, Q20, Q21, Q22, Q23, Q24, Q25, Q26, Q27, Q28, Q29]), "axis" : qUnion([Q30]), "angle" : 70 * degree, "instanceCount" : 2, "oppositeDirection" : true, "patternType" : PatternType.FACE});
        }
        {
            var Q0;
            Q0=makeQuery(id+"F9.opPattern","COPY",FACE,{"derivedFrom":makeQuery(id+"F3.boolean.opBoolean","COPY",FACE,{"derivedFrom":makeQuery(id+"F3.opExtrude","SWEPT_FACE",FACE,{"disambiguationData":[OSD([sQuery(id+"F2.wireOp",EDGE,"E18.13.0")])]})}),"instanceName":"1"});
            var Q1;
            Q1=makeQuery(id+"F9.opPattern","COPY",FACE,{"derivedFrom":makeQuery(id+"F3.boolean.opBoolean","COPY",FACE,{"derivedFrom":makeQuery(id+"F3.opExtrude","SWEPT_FACE",FACE,{"disambiguationData":[OSD([sQuery(id+"F2.wireOp",EDGE,"E18.12.0")])]})}),"instanceName":"1"});
            var Q2;
            Q2=makeQuery(id+"F9.opPattern","COPY",FACE,{"derivedFrom":makeQuery(id+"F3.boolean.opBoolean","COPY",FACE,{"derivedFrom":makeQuery(id+"F3.opExtrude","SWEPT_FACE",FACE,{"disambiguationData":[OSD([sQuery(id+"F2.wireOp",EDGE,"E18.11.0")])]})}),"instanceName":"1"});
            var Q3;
            Q3=makeQuery(id+"F9.opPattern","COPY",FACE,{"derivedFrom":makeQuery(id+"F3.boolean.opBoolean","COPY",FACE,{"derivedFrom":makeQuery(id+"F3.opExtrude","SWEPT_FACE",FACE,{"disambiguationData":[OSD([sQuery(id+"F2.wireOp",EDGE,"E18.10.0")])]})}),"instanceName":"1"});
            var Q4;
            Q4=makeQuery(id+"F9.opPattern","COPY",FACE,{"derivedFrom":makeQuery(id+"F3.boolean.opBoolean","COPY",FACE,{"derivedFrom":makeQuery(id+"F3.opExtrude","SWEPT_FACE",FACE,{"disambiguationData":[OSD([sQuery(id+"F2.wireOp",EDGE,"E18.9.0")])]})}),"instanceName":"1"});
            var Q5;
            Q5=makeQuery(id+"F9.opPattern","COPY",FACE,{"derivedFrom":makeQuery(id+"F3.boolean.opBoolean","COPY",FACE,{"derivedFrom":makeQuery(id+"F3.opExtrude","SWEPT_FACE",FACE,{"disambiguationData":[OSD([sQuery(id+"F2.wireOp",EDGE,"E18.8.0")])]})}),"instanceName":"1"});
            var Q6;
            Q6=makeQuery(id+"F9.opPattern","COPY",FACE,{"derivedFrom":makeQuery(id+"F3.boolean.opBoolean","COPY",FACE,{"derivedFrom":makeQuery(id+"F3.opExtrude","SWEPT_FACE",FACE,{"disambiguationData":[OSD([sQuery(id+"F2.wireOp",EDGE,"E18.7.0")])]})}),"instanceName":"1"});
            var Q7;
            Q7=makeQuery(id+"F9.opPattern","COPY",FACE,{"derivedFrom":makeQuery(id+"F3.boolean.opBoolean","COPY",FACE,{"derivedFrom":makeQuery(id+"F3.opExtrude","SWEPT_FACE",FACE,{"disambiguationData":[OSD([sQuery(id+"F2.wireOp",EDGE,"E18.6.0")])]})}),"instanceName":"1"});
            var Q8;
            Q8=makeQuery(id+"F9.opPattern","COPY",FACE,{"derivedFrom":makeQuery(id+"F3.boolean.opBoolean","COPY",FACE,{"derivedFrom":makeQuery(id+"F3.opExtrude","SWEPT_FACE",FACE,{"disambiguationData":[OSD([sQuery(id+"F2.wireOp",EDGE,"E18.5.0")])]})}),"instanceName":"1"});
            var Q9;
            Q9=makeQuery(id+"F9.opPattern","COPY",FACE,{"derivedFrom":makeQuery(id+"F3.boolean.opBoolean","COPY",FACE,{"derivedFrom":makeQuery(id+"F3.opExtrude","SWEPT_FACE",FACE,{"disambiguationData":[OSD([sQuery(id+"F2.wireOp",EDGE,"E18.4.0")])]})}),"instanceName":"1"});
            var Q10;
            Q10=makeQuery(id+"F9.opPattern","COPY",FACE,{"derivedFrom":makeQuery(id+"F3.boolean.opBoolean","COPY",FACE,{"derivedFrom":makeQuery(id+"F3.opExtrude","SWEPT_FACE",FACE,{"disambiguationData":[OSD([sQuery(id+"F2.wireOp",EDGE,"E18.3.0")])]})}),"instanceName":"1"});
            var Q11;
            Q11=makeQuery(id+"F9.opPattern","COPY",FACE,{"derivedFrom":makeQuery(id+"F3.boolean.opBoolean","COPY",FACE,{"derivedFrom":makeQuery(id+"F3.opExtrude","SWEPT_FACE",FACE,{"disambiguationData":[OSD([sQuery(id+"F2.wireOp",EDGE,"E18.2.0")])]})}),"instanceName":"1"});
            var Q12;
            Q12=makeQuery(id+"F9.opPattern","COPY",FACE,{"derivedFrom":makeQuery(id+"F3.boolean.opBoolean","COPY",FACE,{"derivedFrom":makeQuery(id+"F3.opExtrude","SWEPT_FACE",FACE,{"disambiguationData":[OSD([sQuery(id+"F2.wireOp",EDGE,"E18.1.0")])]})}),"instanceName":"1"});
            var Q13;
            Q13=makeQuery(id+"F9.opPattern","COPY",FACE,{"derivedFrom":makeQuery(id+"F3.boolean.opBoolean","COPY",FACE,{"derivedFrom":makeQuery(id+"F3.opExtrude","SWEPT_FACE",FACE,{"disambiguationData":[OSD([sQuery(id+"F2.wireOp",EDGE,"E17")])]})}),"instanceName":"1"});
            var Q14;
            Q14=makeQuery(id+"F9.opPattern","COPY",FACE,{"derivedFrom":makeQuery(id+"F3.boolean.opBoolean","COPY",FACE,{"derivedFrom":makeQuery(id+"F3.opExtrude","SWEPT_FACE",FACE,{"disambiguationData":[OSD([sQuery(id+"F2.wireOp",EDGE,"E18.14.0")])]})}),"instanceName":"1"});
            var Q15;
            Q15=makeQuery(id+"F9.opPattern","COPY",FACE,{"derivedFrom":makeQuery(id+"F3.boolean.opBoolean","COPY",FACE,{"derivedFrom":makeQuery(id+"F3.opExtrude","SWEPT_FACE",FACE,{"disambiguationData":[OSD([sQuery(id+"F2.wireOp",EDGE,"E11")])]})}),"instanceName":"1"});
            var Q16;
            Q16=makeQuery(id+"F9.opPattern","COPY",FACE,{"derivedFrom":makeQuery(id+"F3.boolean.opBoolean","COPY",FACE,{"derivedFrom":makeQuery(id+"F3.opExtrude","SWEPT_FACE",FACE,{"disambiguationData":[OSD([sQuery(id+"F2.wireOp",EDGE,"E13.1.8.0")])]})}),"instanceName":"1"});
            var Q17;
            Q17=makeQuery(id+"F9.opPattern","COPY",FACE,{"derivedFrom":makeQuery(id+"F3.boolean.opBoolean","COPY",FACE,{"derivedFrom":makeQuery(id+"F3.opExtrude","SWEPT_FACE",FACE,{"disambiguationData":[OSD([sQuery(id+"F2.wireOp",EDGE,"E13.1.7.0")])]})}),"instanceName":"1"});
            var Q18;
            Q18=makeQuery(id+"F9.opPattern","COPY",FACE,{"derivedFrom":makeQuery(id+"F3.boolean.opBoolean","COPY",FACE,{"derivedFrom":makeQuery(id+"F3.opExtrude","SWEPT_FACE",FACE,{"disambiguationData":[OSD([sQuery(id+"F2.wireOp",EDGE,"E12.6.0")])]})}),"instanceName":"1"});
            var Q19;
            Q19=makeQuery(id+"F9.opPattern","COPY",FACE,{"derivedFrom":makeQuery(id+"F3.boolean.opBoolean","COPY",FACE,{"derivedFrom":makeQuery(id+"F3.opExtrude","SWEPT_FACE",FACE,{"disambiguationData":[OSD([sQuery(id+"F2.wireOp",EDGE,"E12.5.0")])]})}),"instanceName":"1"});
            var Q20;
            Q20=makeQuery(id+"F9.opPattern","COPY",FACE,{"derivedFrom":makeQuery(id+"F3.boolean.opBoolean","COPY",FACE,{"derivedFrom":makeQuery(id+"F3.opExtrude","SWEPT_FACE",FACE,{"disambiguationData":[OSD([sQuery(id+"F2.wireOp",EDGE,"E12.4.0")])]})}),"instanceName":"1"});
            var Q21;
            Q21=makeQuery(id+"F9.opPattern","COPY",FACE,{"derivedFrom":makeQuery(id+"F3.boolean.opBoolean","COPY",FACE,{"derivedFrom":makeQuery(id+"F3.opExtrude","SWEPT_FACE",FACE,{"disambiguationData":[OSD([sQuery(id+"F2.wireOp",EDGE,"E12.3.0")])]})}),"instanceName":"1"});
            var Q22;
            Q22=makeQuery(id+"F9.opPattern","COPY",FACE,{"derivedFrom":makeQuery(id+"F3.boolean.opBoolean","COPY",FACE,{"derivedFrom":makeQuery(id+"F3.opExtrude","SWEPT_FACE",FACE,{"disambiguationData":[OSD([sQuery(id+"F2.wireOp",EDGE,"E12.2.0")])]})}),"instanceName":"1"});
            var Q23;
            Q23=makeQuery(id+"F9.opPattern","COPY",FACE,{"derivedFrom":makeQuery(id+"F3.boolean.opBoolean","COPY",FACE,{"derivedFrom":makeQuery(id+"F3.opExtrude","SWEPT_FACE",FACE,{"disambiguationData":[OSD([sQuery(id+"F2.wireOp",EDGE,"E12.1.0")])]})}),"instanceName":"1"});
            var Q24;
            Q24=makeQuery(id+"F9.opPattern","COPY",FACE,{"derivedFrom":makeQuery(id+"F3.boolean.opBoolean","COPY",FACE,{"derivedFrom":makeQuery(id+"F3.opExtrude","SWEPT_FACE",FACE,{"disambiguationData":[OSD([sQuery(id+"F2.wireOp",EDGE,"E6")])]})}),"instanceName":"1"});
            var Q25;
            Q25=makeQuery(id+"F9.opPattern","COPY",FACE,{"derivedFrom":makeQuery(id+"F3.boolean.opBoolean","COPY",FACE,{"derivedFrom":makeQuery(id+"F3.opExtrude","SWEPT_FACE",FACE,{"disambiguationData":[OSD([sQuery(id+"F2.wireOp",EDGE,"E7.4.0")])]})}),"instanceName":"1"});
            var Q26;
            Q26=makeQuery(id+"F9.opPattern","COPY",FACE,{"derivedFrom":makeQuery(id+"F3.boolean.opBoolean","COPY",FACE,{"derivedFrom":makeQuery(id+"F3.opExtrude","SWEPT_FACE",FACE,{"disambiguationData":[OSD([sQuery(id+"F2.wireOp",EDGE,"E7.3.0")])]})}),"instanceName":"1"});
            var Q27;
            Q27=makeQuery(id+"F9.opPattern","COPY",FACE,{"derivedFrom":makeQuery(id+"F3.boolean.opBoolean","COPY",FACE,{"derivedFrom":makeQuery(id+"F3.opExtrude","SWEPT_FACE",FACE,{"disambiguationData":[OSD([sQuery(id+"F2.wireOp",EDGE,"E7.2.0")])]})}),"instanceName":"1"});
            var Q28;
            Q28=makeQuery(id+"F9.opPattern","COPY",FACE,{"derivedFrom":makeQuery(id+"F3.boolean.opBoolean","COPY",FACE,{"derivedFrom":makeQuery(id+"F3.opExtrude","SWEPT_FACE",FACE,{"disambiguationData":[OSD([sQuery(id+"F2.wireOp",EDGE,"E7.1.0")])]})}),"instanceName":"1"});
            var Q29;
            Q29=makeQuery(id+"F9.opPattern","COPY",FACE,{"derivedFrom":makeQuery(id+"F3.boolean.opBoolean","COPY",FACE,{"derivedFrom":makeQuery(id+"F3.opExtrude","SWEPT_FACE",FACE,{"disambiguationData":[OSD([sQuery(id+"F2.wireOp",EDGE,"E5")])]})}),"instanceName":"1"});
            var Q30;
            Q30=sQuery(id+"F0.wireOp",EDGE,"E2");
            circularPattern(context, id + "F10", {"faces" : qUnion([Q0, Q1, Q2, Q3, Q4, Q5, Q6, Q7, Q8, Q9, Q10, Q11, Q12, Q13, Q14, Q15, Q16, Q17, Q18, Q19, Q20, Q21, Q22, Q23, Q24, Q25, Q26, Q27, Q28, Q29]), "axis" : qUnion([Q30]), "angle" : 360 * degree, "instanceCount" : 13, "equalSpace" : true, "patternType" : PatternType.FACE});
        }
    });
